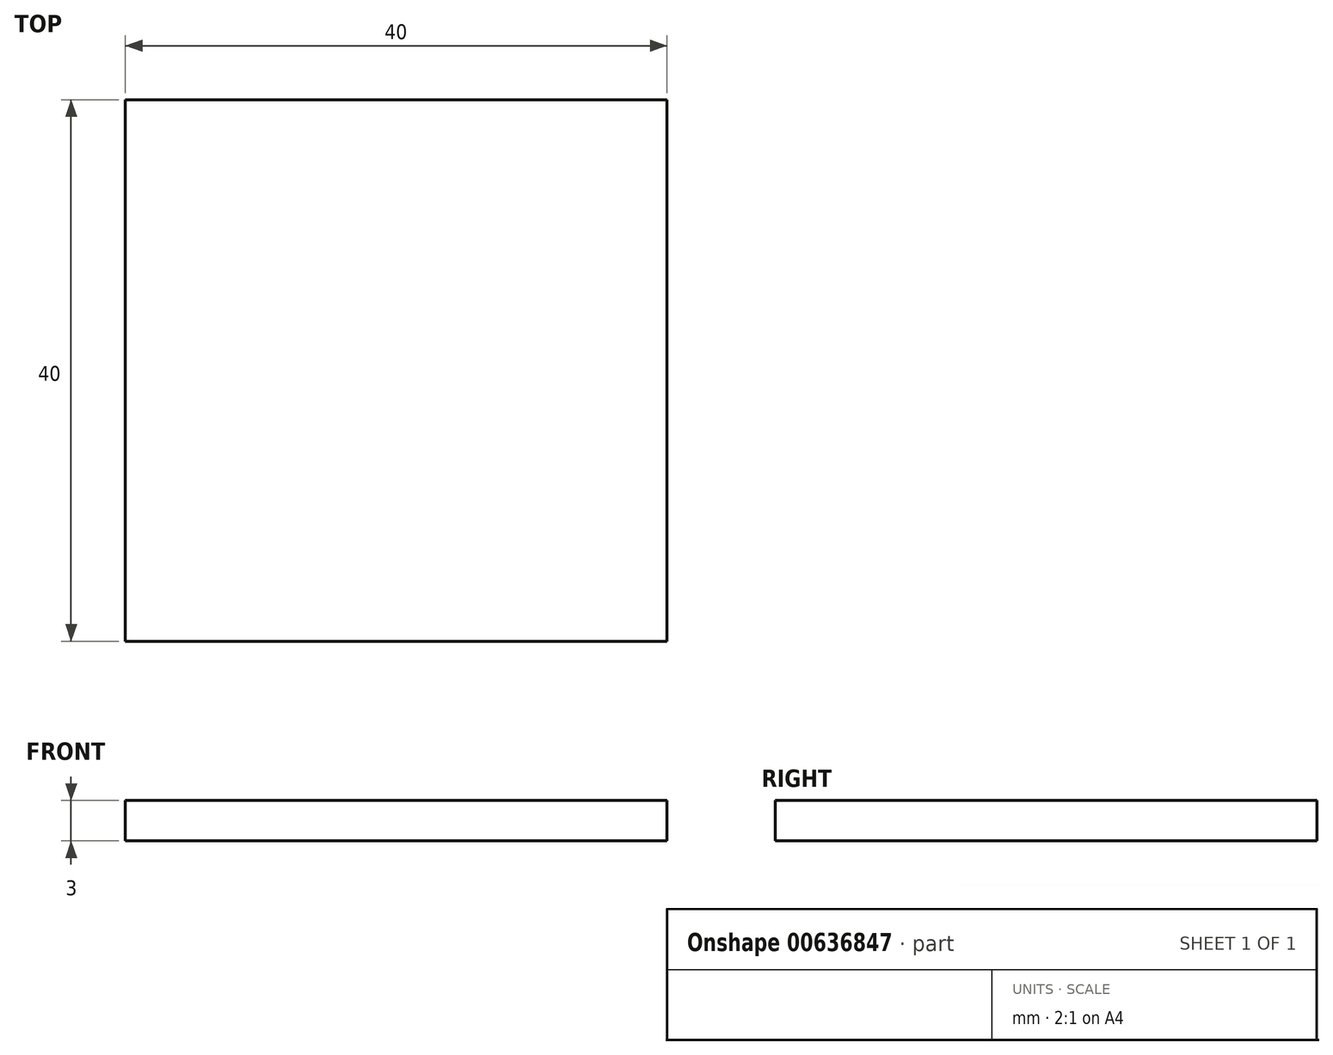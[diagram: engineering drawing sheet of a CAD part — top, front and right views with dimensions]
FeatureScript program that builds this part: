
annotation { "Feature Type Name" : "Feature", "Feature Type Description" : "" }
export const myFeature = defineFeature(function(context is Context, id is Id, definition is map)
    precondition{}
    {
        {
            var Q0;
            Q0=qCreatedBy(makeId("Top.planeOp"),FACE);
            var sketch = newSketch(context, id + "F0", { "sketchPlane" : qUnion([Q0])});
            skLineSegment(sketch, "E0.bottom", {"start": v(20, -20) * mm, "end": v(-20, -20) * mm});
            skLineSegment(sketch, "E0.top", {"start": v(20, 20) * mm, "end": v(-20, 20) * mm});
            skLineSegment(sketch, "E0.left", {"start": v(20, -20) * mm, "end": v(20, 20) * mm});
            skLineSegment(sketch, "E0.right", {"start": v(-20, -20) * mm, "end": v(-20, 20) * mm});
            skPoint(sketch, "E0.middle", {"position": v(0, 0) * mm});
            skSolve(sketch);
        }
        {
            var Q0;
            Q0=makeQuery(id+"F0.imprint","IMPRINT",FACE,{"disambiguationData":[TD([[makeQuery(id+"F0.imprint","IMPRINT",EDGE,{"derivedFrom":sQuery(id+"F0.wireOp",EDGE,"E0.bottom")}),-1.0]])]});
            extrude(context, id + "F1", {"entities" : qUnion([Q0]), "depth" : 3 * mm, "offsetDistance" : 25 * mm});
        }
    });
